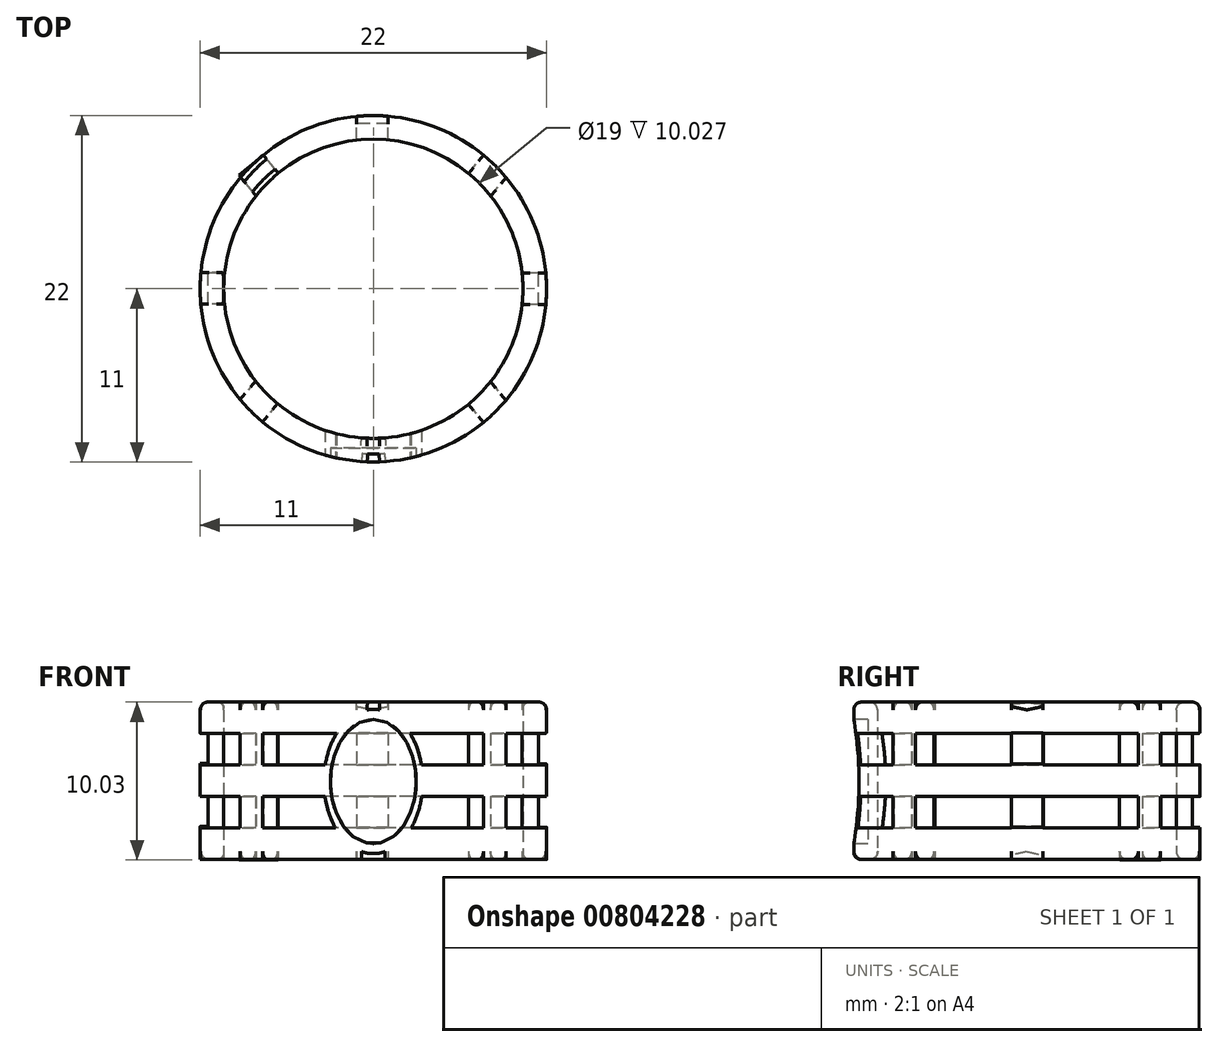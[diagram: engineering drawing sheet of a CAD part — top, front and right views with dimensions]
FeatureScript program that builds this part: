
annotation { "Feature Type Name" : "Feature", "Feature Type Description" : "" }
export const myFeature = defineFeature(function(context is Context, id is Id, definition is map)
    precondition{}
    {
        {
            var Q0;
            Q0=qCreatedBy(makeId("Top.planeOp"),FACE);
            var sketch = newSketch(context, id + "F0", { "sketchPlane" : qUnion([Q0])});
            skCircle(sketch, "E0", {"center": v(0, 0) * mm, "radius": 9.5 * mm});
            skCircle(sketch, "E1", {"center": v(0, 0) * mm, "radius": 11 * mm});
            skSolve(sketch);
        }
        {
            var Q0;
            Q0=makeQuery(id+"F0.imprint","IMPRINT",FACE,{"disambiguationData":[TD([[makeQuery(id+"F0.imprint","IMPRINT",EDGE,{"derivedFrom":sQuery(id+"F0.wireOp",EDGE,"E0")}),-1.0]])]});
            extrude(context, id + "F1", {"entities" : qUnion([Q0]), "depth" : 2 * mm, "offsetDistance" : 25.4 * mm});
        }
        {
            var Q0;
            Q0=qCreatedBy(makeId("Top.planeOp"),FACE);
            cPlane(context, id + "F2", {"entities" : qUnion([Q0]), "cplaneType" : CPlaneType.OFFSET, "offset" : 4 * mm, "width" : 152.4 * mm, "height" : 152.4 * mm});
        }
        {
            var Q0;
            Q0=qCreatedBy(id+"F2.planeOp",FACE);
            var sketch = newSketch(context, id + "F3", { "sketchPlane" : qUnion([Q0])});
            skCircle(sketch, "E2", {"center": v(0, 0) * mm, "radius": 9.5 * mm});
            skCircle(sketch, "E3", {"center": v(0, 0) * mm, "radius": 11 * mm});
            skSolve(sketch);
        }
        {
            var Q0;
            Q0=makeQuery(id+"F3.imprint","IMPRINT",FACE,{"disambiguationData":[TD([[makeQuery(id+"F3.imprint","IMPRINT",EDGE,{"derivedFrom":sQuery(id+"F3.wireOp",EDGE,"E2")}),-1.0]])]});
            extrude(context, id + "F4", {"entities" : qUnion([Q0]), "depth" : 2 * mm, "offsetDistance" : 25.4 * mm});
        }
        {
            var Q0;
            Q0=qCreatedBy(id+"F2.planeOp",FACE);
            cPlane(context, id + "F5", {"entities" : qUnion([Q0]), "cplaneType" : CPlaneType.OFFSET, "offset" : 4 * mm, "width" : 152.4 * mm, "height" : 152.4 * mm});
        }
        {
            var Q0;
            Q0=qCreatedBy(id+"F5.planeOp",FACE);
            var sketch = newSketch(context, id + "F6", { "sketchPlane" : qUnion([Q0])});
            skCircle(sketch, "E4", {"center": v(0, 0) * mm, "radius": 9.5 * mm});
            skCircle(sketch, "E5", {"center": v(0, 0) * mm, "radius": 11 * mm});
            skSolve(sketch);
        }
        {
            var Q0;
            Q0 = qSketchRegion(id + "F6", true);
            extrude(context, id + "F7", {"entities" : qUnion([Q0]), "depth" : 2 * mm, "offsetDistance" : 25.4 * mm});
        }
        {
            var Q0;
            Q0=qCreatedBy(makeId("Front.planeOp"),FACE);
            cPlane(context, id + "F8", {"entities" : qUnion([Q0]), "cplaneType" : CPlaneType.OFFSET, "offset" : 11 * mm, "width" : 152.4 * mm, "height" : 152.4 * mm});
        }
        {
            var Q0;
            Q0=qCreatedBy(id+"F8.planeOp",FACE);
            var sketch = newSketch(context, id + "F9", { "sketchPlane" : qUnion([Q0])});
            skEllipse(sketch, "E6", {"center": v(0, 4.95) * mm, "majorRadius": 4.58 * mm, "minorRadius": 3.14 * mm, "majorAxis": v(0, 1)});
            skEllipse(sketch, "E7", {"center": v(0, 4.95) * mm, "majorRadius": 4.36 * mm, "minorRadius": 2.48 * mm, "majorAxis": v(0, 1)});
            skSolve(sketch);
        }
        {
            var Q0;
            Q0=makeQuery(id+"F9.imprint","IMPRINT",FACE,{"disambiguationData":[TD([[makeQuery(id+"F9.imprint","IMPRINT",EDGE,{"derivedFrom":sQuery(id+"F9.wireOp",EDGE,"E7")}),1.0]])]});
            var Q1;
            Q1=makeQuery(id+"F9.imprint","IMPRINT",FACE,{"disambiguationData":[TD([[makeQuery(id+"F9.imprint","IMPRINT",EDGE,{"derivedFrom":sQuery(id+"F9.wireOp",EDGE,"E6")}),1.0]])]});
            extrude(context, id + "F10", {"entities" : qUnion([Q0, Q1]), "operationType" : NewBodyOperationType.ADD, "oppositeDirection" : true, "depth" : 2 * mm, "offsetDistance" : 25.4 * mm});
        }
        {
            var Q0;
            Q0=makeQuery(id+"F10.opExtrude","CAP_FACE",FACE,{"disambiguationData":[OSD([sQuery(id+"F9.wireOp",EDGE,"E6")])],"isStart":true});
            var sketch = newSketch(context, id + "F11", { "sketchPlane" : qUnion([Q0])});
            skEllipse(sketch, "E8", {"center": v(0, 4.95) * mm, "majorRadius": 3.96 * mm, "minorRadius": 2.72 * mm, "majorAxis": v(0, 1)});
            skSolve(sketch);
        }
        {
            var Q0;
            Q0=makeQuery(id+"F11.imprint","IMPRINT",FACE,{"disambiguationData":[TD([[makeQuery(id+"F11.imprint","IMPRINT",EDGE,{"derivedFrom":sQuery(id+"F11.wireOp",EDGE,"E8")}),1.0]])]});
            extrude(context, id + "F12", {"entities" : qUnion([Q0]), "operationType" : NewBodyOperationType.REMOVE, "oppositeDirection" : true, "depth" : .9 * mm, "offsetDistance" : 25.4 * mm});
        }
        {
            var Q0;
            Q0=qCreatedBy(makeId("Front.planeOp"),FACE);
            cPlane(context, id + "F13", {"entities" : qUnion([Q0]), "cplaneType" : CPlaneType.OFFSET, "offset" : 11 * mm, "oppositeDirection" : true, "width" : 152.4 * mm, "height" : 152.4 * mm});
        }
        {
            var Q0;
            Q0=qCreatedBy(id+"F13.planeOp",FACE);
            var sketch = newSketch(context, id + "F14", { "sketchPlane" : qUnion([Q0])});
            skLineSegment(sketch, "E9.bottom", {"start": v(0.94, 10) * mm, "end": v(-1.06, 10) * mm});
            skLineSegment(sketch, "E9.top", {"start": v(0.94, 0) * mm, "end": v(-1.06, 0) * mm});
            skLineSegment(sketch, "E9.left", {"start": v(0.94, 10) * mm, "end": v(0.94, 0) * mm});
            skLineSegment(sketch, "E9.right", {"start": v(-1.06, 10) * mm, "end": v(-1.06, 0) * mm});
            skSolve(sketch);
        }
        {
            var Q0;
            Q0=makeQuery(id+"F14.imprint","IMPRINT",FACE,{"disambiguationData":[TD([[makeQuery(id+"F14.imprint","IMPRINT",EDGE,{"derivedFrom":sQuery(id+"F14.wireOp",EDGE,"E9.bottom")}),1.0]])]});
            extrude(context, id + "F15", {"entities" : qUnion([Q0]), "operationType" : NewBodyOperationType.ADD, "depth" : 1.5 * mm, "offsetDistance" : 25.4 * mm});
        }
        {
            var Q0;
            Q0=makeQuery(id+"F7.opExtrude","CAP_EDGE",EDGE,{"disambiguationData":[OSD([sQuery(id+"F6.wireOp",EDGE,"E4")])],"isStart":false});
            var Q1;
            Q1=makeQuery(id+"F7.opExtrude","CAP_EDGE",EDGE,{"disambiguationData":[OSD([sQuery(id+"F6.wireOp",EDGE,"E5")])],"isStart":false});
            var Q2;
            Q2=makeQuery(id+"F1.opExtrude","CAP_EDGE",EDGE,{"disambiguationData":[OSD([sQuery(id+"F0.wireOp",EDGE,"E1")])],"isStart":true});
            var Q3;
            Q3=makeQuery(id+"F1.opExtrude","CAP_EDGE",EDGE,{"disambiguationData":[OSD([sQuery(id+"F0.wireOp",EDGE,"E0")])],"isStart":true});
            fillet(context, id + "F16", {"entities" : qUnion([Q0, Q1, Q2, Q3]), "radius" : .5 * mm, "tangentPropagation" : true, "allowEdgeOverflow" : false});
        }
        {
            var Q0;
            Q0=makeQuery(id+"F15.opExtrude","CAP_EDGE",EDGE,{"disambiguationData":[OSD([sQuery(id+"F14.wireOp",EDGE,"E9.bottom")])],"isStart":true});
            fillet(context, id + "F17", {"entities" : qUnion([Q0]), "radius" : .5 * mm, "tangentPropagation" : true, "allowEdgeOverflow" : false});
        }
        {
            var Q0;
            Q0=qCreatedBy(makeId("Right.planeOp"),FACE);
            cPlane(context, id + "F18", {"entities" : qUnion([Q0]), "cplaneType" : CPlaneType.OFFSET, "offset" : 11 * mm, "width" : 152.4 * mm, "height" : 152.4 * mm});
        }
        {
            var Q0;
            Q0=qCreatedBy(id+"F18.planeOp",FACE);
            var sketch = newSketch(context, id + "F19", { "sketchPlane" : qUnion([Q0])});
            skLineSegment(sketch, "E10.bottom", {"start": v(-1, 0) * mm, "end": v(1, 0) * mm});
            skLineSegment(sketch, "E10.top", {"start": v(-1, 10) * mm, "end": v(1, 10) * mm});
            skLineSegment(sketch, "E10.left", {"start": v(-1, 0) * mm, "end": v(-1, 10) * mm});
            skLineSegment(sketch, "E10.right", {"start": v(1, 0) * mm, "end": v(1, 10) * mm});
            skSolve(sketch);
        }
        {
            var Q0;
            Q0=makeQuery(id+"F19.imprint","IMPRINT",FACE,{"disambiguationData":[TD([[makeQuery(id+"F19.imprint","IMPRINT",EDGE,{"derivedFrom":sQuery(id+"F19.wireOp",EDGE,"E10.bottom")}),1.0]])]});
            extrude(context, id + "F20", {"entities" : qUnion([Q0]), "operationType" : NewBodyOperationType.ADD, "oppositeDirection" : true, "depth" : 1.7 * mm, "offsetDistance" : 25.4 * mm});
        }
        {
            var Q0;
            Q0=qCreatedBy(makeId("Right.planeOp"),FACE);
            cPlane(context, id + "F21", {"entities" : qUnion([Q0]), "cplaneType" : CPlaneType.OFFSET, "offset" : 11 * mm, "oppositeDirection" : true, "width" : 152.4 * mm, "height" : 152.4 * mm});
        }
        {
            var Q0;
            Q0=qCreatedBy(id+"F21.planeOp",FACE);
            var sketch = newSketch(context, id + "F22", { "sketchPlane" : qUnion([Q0])});
            skLineSegment(sketch, "E11.bottom", {"start": v(1.04, 10) * mm, "end": v(-0.96, 10) * mm});
            skLineSegment(sketch, "E11.top", {"start": v(1.04, 0) * mm, "end": v(-0.96, 0) * mm});
            skLineSegment(sketch, "E11.left", {"start": v(1.04, 10) * mm, "end": v(1.04, 0) * mm});
            skLineSegment(sketch, "E11.right", {"start": v(-0.96, 10) * mm, "end": v(-0.96, 0) * mm});
            skSolve(sketch);
        }
        {
            var Q0;
            Q0=makeQuery(id+"F22.imprint","IMPRINT",FACE,{"disambiguationData":[TD([[makeQuery(id+"F22.imprint","IMPRINT",EDGE,{"derivedFrom":sQuery(id+"F22.wireOp",EDGE,"E11.bottom")}),1.0]])]});
            extrude(context, id + "F23", {"entities" : qUnion([Q0]), "operationType" : NewBodyOperationType.ADD, "depth" : 1.5 * mm, "offsetDistance" : 25.4 * mm});
        }
        {
            var Q0;
            Q0=makeQuery(id+"F20.opExtrude","CAP_EDGE",EDGE,{"disambiguationData":[OSD([sQuery(id+"F19.wireOp",EDGE,"E10.top")])],"isStart":false});
            var Q1;
            Q1=makeQuery(id+"F20.opExtrude","CAP_EDGE",EDGE,{"disambiguationData":[OSD([sQuery(id+"F19.wireOp",EDGE,"E10.top")])],"isStart":true});
            var Q2;
            Q2=makeQuery(id+"F23.opExtrude","CAP_EDGE",EDGE,{"disambiguationData":[OSD([sQuery(id+"F22.wireOp",EDGE,"E11.bottom")])],"isStart":true});
            fillet(context, id + "F24", {"entities" : qUnion([Q0, Q1, Q2]), "radius" : .5 * mm, "tangentPropagation" : true, "allowEdgeOverflow" : false});
        }
        {
            var Q0;
            Q0=makeQuery(id+"F23.opExtrude","CAP_EDGE",EDGE,{"disambiguationData":[OSD([sQuery(id+"F22.wireOp",EDGE,"E11.bottom")])],"isStart":false});
            fillet(context, id + "F25", {"entities" : qUnion([Q0]), "radius" : .4 * mm, "tangentPropagation" : true, "allowEdgeOverflow" : false});
        }
        {
            var Q0;
            Q0=makeQuery(id+"F20.opExtrude","CAP_FACE",FACE,{"disambiguationData":[OSD([sQuery(id+"F19.wireOp",EDGE,"E10.bottom"),sQuery(id+"F19.wireOp",EDGE,"E10.top"),sQuery(id+"F19.wireOp",EDGE,"E10.left"),sQuery(id+"F19.wireOp",EDGE,"E10.right")])],"isStart":true});
            var sketch = newSketch(context, id + "F26", { "sketchPlane" : qUnion([Q0])});
            skLineSegment(sketch, "E12.bottom", {"start": v(-1, 8.03) * mm, "end": v(1, 8.03) * mm});
            skLineSegment(sketch, "E12.top", {"start": v(-1, 6.06) * mm, "end": v(1, 6.06) * mm});
            skLineSegment(sketch, "E12.left", {"start": v(-1, 8.03) * mm, "end": v(-1, 6.06) * mm});
            skLineSegment(sketch, "E12.right", {"start": v(1, 8.03) * mm, "end": v(1, 6.06) * mm});
            skLineSegment(sketch, "E13.bottom", {"start": v(-1, 4.02) * mm, "end": v(1, 4.02) * mm});
            skLineSegment(sketch, "E13.top", {"start": v(-1, 2.05) * mm, "end": v(1, 2.05) * mm});
            skLineSegment(sketch, "E13.left", {"start": v(-1, 4.02) * mm, "end": v(-1, 2.05) * mm});
            skLineSegment(sketch, "E13.right", {"start": v(1, 4.02) * mm, "end": v(1, 2.05) * mm});
            skSolve(sketch);
        }
        {
            var Q0;
            Q0=makeQuery(id+"F26.imprint","IMPRINT",FACE,{"disambiguationData":[TD([[makeQuery(id+"F26.imprint","IMPRINT",EDGE,{"derivedFrom":sQuery(id+"F26.wireOp",EDGE,"E12.bottom")}),-1.0]])]});
            var Q1;
            Q1=makeQuery(id+"F26.imprint","IMPRINT",FACE,{"disambiguationData":[TD([[makeQuery(id+"F26.imprint","IMPRINT",EDGE,{"derivedFrom":sQuery(id+"F26.wireOp",EDGE,"E13.bottom")}),-1.0]])]});
            extrude(context, id + "F27", {"entities" : qUnion([Q0, Q1]), "operationType" : NewBodyOperationType.REMOVE, "oppositeDirection" : true, "depth" : .5 * mm, "offsetDistance" : 25.4 * mm});
        }
        {
            var Q0;
            Q0=makeQuery(id+"F15.opExtrude","CAP_FACE",FACE,{"disambiguationData":[OSD([sQuery(id+"F14.wireOp",EDGE,"E9.bottom"),sQuery(id+"F14.wireOp",EDGE,"E9.top"),sQuery(id+"F14.wireOp",EDGE,"E9.left"),sQuery(id+"F14.wireOp",EDGE,"E9.right")])],"isStart":true});
            var sketch = newSketch(context, id + "F28", { "sketchPlane" : qUnion([Q0])});
            skLineSegment(sketch, "E14.bottom", {"start": v(-0.94, 8.03) * mm, "end": v(1.06, 8.03) * mm});
            skLineSegment(sketch, "E14.top", {"start": v(-0.94, 6.01) * mm, "end": v(1.06, 6.01) * mm});
            skLineSegment(sketch, "E14.left", {"start": v(-0.94, 8.03) * mm, "end": v(-0.94, 6.01) * mm});
            skLineSegment(sketch, "E14.right", {"start": v(1.06, 8.03) * mm, "end": v(1.06, 6.01) * mm});
            skLineSegment(sketch, "E15.bottom", {"start": v(1.06, 4) * mm, "end": v(-0.94, 4) * mm});
            skLineSegment(sketch, "E15.top", {"start": v(1.06, 2.05) * mm, "end": v(-0.94, 2.05) * mm});
            skLineSegment(sketch, "E15.left", {"start": v(1.06, 4) * mm, "end": v(1.06, 2.05) * mm});
            skLineSegment(sketch, "E15.right", {"start": v(-0.94, 4) * mm, "end": v(-0.94, 2.05) * mm});
            skSolve(sketch);
        }
        {
            var Q0;
            Q0=makeQuery(id+"F28.imprint","IMPRINT",FACE,{"disambiguationData":[TD([[makeQuery(id+"F28.imprint","IMPRINT",EDGE,{"derivedFrom":sQuery(id+"F28.wireOp",EDGE,"E14.bottom")}),-1.0]])]});
            var Q1;
            Q1=makeQuery(id+"F28.imprint","IMPRINT",FACE,{"disambiguationData":[TD([[makeQuery(id+"F28.imprint","IMPRINT",EDGE,{"derivedFrom":sQuery(id+"F28.wireOp",EDGE,"E15.bottom")}),1.0]])]});
            extrude(context, id + "F29", {"entities" : qUnion([Q0, Q1]), "operationType" : NewBodyOperationType.REMOVE, "oppositeDirection" : true, "depth" : .5 * mm, "offsetDistance" : 25.4 * mm});
        }
        {
            var Q0;
            Q0=makeQuery(id+"F23.opExtrude","CAP_FACE",FACE,{"disambiguationData":[OSD([sQuery(id+"F22.wireOp",EDGE,"E11.bottom"),sQuery(id+"F22.wireOp",EDGE,"E11.top"),sQuery(id+"F22.wireOp",EDGE,"E11.left"),sQuery(id+"F22.wireOp",EDGE,"E11.right")])],"isStart":true});
            var sketch = newSketch(context, id + "F30", { "sketchPlane" : qUnion([Q0])});
            skLineSegment(sketch, "E16.bottom", {"start": v(-1.04, 8) * mm, "end": v(0.96, 8) * mm});
            skLineSegment(sketch, "E16.top", {"start": v(-1.04, 6.1) * mm, "end": v(0.96, 6.1) * mm});
            skLineSegment(sketch, "E16.left", {"start": v(-1.04, 8) * mm, "end": v(-1.04, 6.1) * mm});
            skLineSegment(sketch, "E16.right", {"start": v(0.96, 8) * mm, "end": v(0.96, 6.1) * mm});
            skLineSegment(sketch, "E17.bottom", {"start": v(0.96, 2.1) * mm, "end": v(-1.04, 2.1) * mm});
            skLineSegment(sketch, "E17.top", {"start": v(0.96, 4) * mm, "end": v(-1.04, 4) * mm});
            skLineSegment(sketch, "E17.left", {"start": v(0.96, 2.1) * mm, "end": v(0.96, 4) * mm});
            skLineSegment(sketch, "E17.right", {"start": v(-1.04, 2.1) * mm, "end": v(-1.04, 4) * mm});
            skSolve(sketch);
        }
        {
            var Q0;
            Q0=makeQuery(id+"F30.imprint","IMPRINT",FACE,{"disambiguationData":[TD([[makeQuery(id+"F30.imprint","IMPRINT",EDGE,{"derivedFrom":sQuery(id+"F30.wireOp",EDGE,"E16.bottom")}),-1.0]])]});
            var Q1;
            Q1=makeQuery(id+"F30.imprint","IMPRINT",FACE,{"disambiguationData":[TD([[makeQuery(id+"F30.imprint","IMPRINT",EDGE,{"derivedFrom":sQuery(id+"F30.wireOp",EDGE,"E17.bottom")}),-1.0]])]});
            extrude(context, id + "F31", {"entities" : qUnion([Q0, Q1]), "operationType" : NewBodyOperationType.REMOVE, "oppositeDirection" : true, "depth" : .5 * mm, "offsetDistance" : 25.4 * mm});
        }
        {
            var Q0;
            Q0=qCreatedBy(makeId("Top.planeOp"),FACE);
            var sketch = newSketch(context, id + "F32", { "sketchPlane" : qUnion([Q0])});
            skCircle(sketch, "E18", {"center": v(0, 0) * mm, "radius": 9.5 * mm});
            skSolve(sketch);
        }
        {
            var Q0;
            Q0=qCreatedBy(makeId("Top.planeOp"),FACE);
            var sketch = newSketch(context, id + "F33", { "sketchPlane" : qUnion([Q0])});
            skCircle(sketch, "E19", {"center": v(0, 0) * mm, "radius": 11 * mm});
            skCircle(sketch, "E20", {"center": v(0, 0) * mm, "radius": 11.5 * mm});
            skSolve(sketch);
        }
        {
            var Q0;
            Q0=makeQuery(id+"F33.imprint","IMPRINT",FACE,{"disambiguationData":[TD([[makeQuery(id+"F33.imprint","IMPRINT",EDGE,{"derivedFrom":sQuery(id+"F33.wireOp",EDGE,"E19")}),-1.0]])]});
            extrude(context, id + "F34", {"entities" : qUnion([Q0]), "operationType" : NewBodyOperationType.REMOVE, "depth" : 25.4 * mm, "offsetDistance" : 25.4 * mm});
        }
        {
            var Q0;
            {var subQ0=sQuery(id+"F3.wireOp",EDGE,"E3");var subQ3=makeQuery(id+"F10.opExtrude","SWEPT_FACE",FACE,{"disambiguationData":[OSD([sQuery(id+"F9.wireOp",EDGE,"E6")])]});Q0=makeQuery(id+"F23.boolean.opBoolean","SPLIT",EDGE,{"disambiguationData":[TD([subQ3])],"derivedFrom":makeQuery(id+"F15.boolean.opBoolean","SPLIT",EDGE,{"disambiguationData":[TD([makeQuery(id+"F15.opExtrude","SWEPT_FACE",FACE,{"disambiguationData":[OSD([sQuery(id+"F14.wireOp",EDGE,"E9.right")])]})])],"derivedFrom":makeQuery(id+"F4.opExtrude","CAP_EDGE",EDGE,{"disambiguationData":[OSD([subQ0])],"isStart":false})})});}
            cPoint(context, id + "F35", {"entities" : qUnion([Q0]), "parameter" : 0.5});
        }
        {
            var Q0;
            {var subQ0=sQuery(id+"F3.wireOp",EDGE,"E3");var subQ3=makeQuery(id+"F10.opExtrude","SWEPT_FACE",FACE,{"disambiguationData":[OSD([sQuery(id+"F9.wireOp",EDGE,"E6")])]});Q0=makeQuery(id+"F23.boolean.opBoolean","SPLIT",EDGE,{"disambiguationData":[TD([subQ3])],"derivedFrom":makeQuery(id+"F15.boolean.opBoolean","SPLIT",EDGE,{"disambiguationData":[TD([makeQuery(id+"F15.opExtrude","SWEPT_FACE",FACE,{"disambiguationData":[OSD([sQuery(id+"F14.wireOp",EDGE,"E9.right")])]})])],"derivedFrom":makeQuery(id+"F4.opExtrude","CAP_EDGE",EDGE,{"disambiguationData":[OSD([subQ0])],"isStart":false})})});}
            var Q1;
            Q1 = qCreatedBy(id + "F35" ,VERTEX);
            cPlane(context, id + "F36", {"entities" : qUnion([Q0, Q1]), "cplaneType" : CPlaneType.CURVE_POINT, "offset" : 25.4 * mm, "width" : 152.4 * mm, "height" : 152.4 * mm});
        }
        {
            var Q0;
            Q0=qCreatedBy(id+"F36.planeOp",FACE);
            cPlane(context, id + "F37", {"entities" : qUnion([Q0]), "cplaneType" : CPlaneType.OFFSET, "offset" : 11 * mm, "oppositeDirection" : true, "width" : 152.4 * mm, "height" : 152.4 * mm});
        }
        {
            var Q0;
            Q0=qCreatedBy(id+"F37.planeOp",FACE);
            var sketch = newSketch(context, id + "F38", { "sketchPlane" : qUnion([Q0])});
            skLineSegment(sketch, "E21.bottom", {"start": v(0, 9.97) * mm, "end": v(-2, 9.97) * mm});
            skLineSegment(sketch, "E21.top", {"start": v(0, -0.03) * mm, "end": v(-2, -0.03) * mm});
            skLineSegment(sketch, "E21.left", {"start": v(0, 9.97) * mm, "end": v(0, -0.03) * mm});
            skLineSegment(sketch, "E21.right", {"start": v(-2, 9.97) * mm, "end": v(-2, -0.03) * mm});
            skSolve(sketch);
        }
        {
            var Q0;
            Q0=makeQuery(id+"F38.imprint","IMPRINT",FACE,{"disambiguationData":[TD([[makeQuery(id+"F38.imprint","IMPRINT",EDGE,{"derivedFrom":sQuery(id+"F38.wireOp",EDGE,"E21.bottom")}),1.0]])]});
            extrude(context, id + "F39", {"entities" : qUnion([Q0]), "operationType" : NewBodyOperationType.ADD, "depth" : 3 * mm, "offsetDistance" : 25.4 * mm});
        }
        {
            var Q0;
            Q0=qCreatedBy(id+"F36.planeOp",FACE);
            cPlane(context, id + "F40", {"entities" : qUnion([Q0]), "cplaneType" : CPlaneType.OFFSET, "offset" : 11 * mm, "width" : 152.4 * mm, "height" : 152.4 * mm});
        }
        {
            var Q0;
            Q0=qCreatedBy(id+"F40.planeOp",FACE);
            var sketch = newSketch(context, id + "F41", { "sketchPlane" : qUnion([Q0])});
            skLineSegment(sketch, "E22.bottom", {"start": v(0, 10) * mm, "end": v(2, 10) * mm});
            skLineSegment(sketch, "E22.top", {"start": v(0, 0) * mm, "end": v(2, 0) * mm});
            skLineSegment(sketch, "E22.left", {"start": v(0, 10) * mm, "end": v(0, 0) * mm});
            skLineSegment(sketch, "E22.right", {"start": v(2, 10) * mm, "end": v(2, 0) * mm});
            skSolve(sketch);
        }
        {
            var Q0;
            {var subQ0=sQuery(id+"F3.wireOp",EDGE,"E3");var subQ3=makeQuery(id+"F10.opExtrude","SWEPT_FACE",FACE,{"disambiguationData":[OSD([sQuery(id+"F9.wireOp",EDGE,"E6")])]});Q0=makeQuery(id+"F20.boolean.opBoolean","SPLIT",EDGE,{"disambiguationData":[TD([subQ3])],"derivedFrom":makeQuery(id+"F15.boolean.opBoolean","SPLIT",EDGE,{"disambiguationData":[TD([makeQuery(id+"F15.opExtrude","SWEPT_FACE",FACE,{"disambiguationData":[OSD([sQuery(id+"F14.wireOp",EDGE,"E9.left")])]})])],"derivedFrom":makeQuery(id+"F4.opExtrude","CAP_EDGE",EDGE,{"disambiguationData":[OSD([subQ0])],"isStart":false})})});}
            cPoint(context, id + "F42", {"entities" : qUnion([Q0]), "parameter" : 0.5});
        }
        {
            var Q0;
            Q0 = qCreatedBy(id + "F42" ,VERTEX);
            var Q1;
            {var subQ0=sQuery(id+"F3.wireOp",EDGE,"E3");var subQ3=makeQuery(id+"F10.opExtrude","SWEPT_FACE",FACE,{"disambiguationData":[OSD([sQuery(id+"F9.wireOp",EDGE,"E6")])]});Q1=makeQuery(id+"F20.boolean.opBoolean","SPLIT",EDGE,{"disambiguationData":[TD([subQ3])],"derivedFrom":makeQuery(id+"F15.boolean.opBoolean","SPLIT",EDGE,{"disambiguationData":[TD([makeQuery(id+"F15.opExtrude","SWEPT_FACE",FACE,{"disambiguationData":[OSD([sQuery(id+"F14.wireOp",EDGE,"E9.left")])]})])],"derivedFrom":makeQuery(id+"F4.opExtrude","CAP_EDGE",EDGE,{"disambiguationData":[OSD([subQ0])],"isStart":false})})});}
            cPlane(context, id + "F43", {"entities" : qUnion([Q0, Q1]), "cplaneType" : CPlaneType.CURVE_POINT, "offset" : 25.4 * mm, "width" : 152.4 * mm, "height" : 152.4 * mm});
        }
        {
            var Q0;
            Q0 = qSketchRegion(id + "F41", true);
            extrude(context, id + "F44", {"entities" : qUnion([Q0]), "operationType" : NewBodyOperationType.ADD, "oppositeDirection" : true, "depth" : 3 * mm, "offsetDistance" : 25.4 * mm});
        }
        {
            var Q0;
            Q0=qCreatedBy(id+"F43.planeOp",FACE);
            cPlane(context, id + "F45", {"entities" : qUnion([Q0]), "cplaneType" : CPlaneType.OFFSET, "offset" : 11 * mm, "oppositeDirection" : true, "width" : 152.4 * mm, "height" : 152.4 * mm});
        }
        {
            var Q0;
            Q0=qCreatedBy(id+"F45.planeOp",FACE);
            var sketch = newSketch(context, id + "F46", { "sketchPlane" : qUnion([Q0])});
            skLineSegment(sketch, "E23.bottom", {"start": v(2.04, 10) * mm, "end": v(0.04, 10) * mm});
            skLineSegment(sketch, "E23.top", {"start": v(2.04, 0) * mm, "end": v(0.04, 0) * mm});
            skLineSegment(sketch, "E23.left", {"start": v(2.04, 10) * mm, "end": v(2.04, 0) * mm});
            skLineSegment(sketch, "E23.right", {"start": v(0.04, 10) * mm, "end": v(0.04, 0) * mm});
            skSolve(sketch);
        }
        {
            var Q0;
            Q0=qCreatedBy(id+"F43.planeOp",FACE);
            cPlane(context, id + "F47", {"entities" : qUnion([Q0]), "cplaneType" : CPlaneType.OFFSET, "offset" : 11 * mm, "width" : 152.4 * mm, "height" : 152.4 * mm});
        }
        {
            var Q0;
            Q0=qCreatedBy(id+"F47.planeOp",FACE);
            var sketch = newSketch(context, id + "F48", { "sketchPlane" : qUnion([Q0])});
            skLineSegment(sketch, "E24.bottom", {"start": v(-2, 10) * mm, "end": v(0, 10) * mm});
            skLineSegment(sketch, "E24.top", {"start": v(-2, 0) * mm, "end": v(0, 0) * mm});
            skLineSegment(sketch, "E24.left", {"start": v(-2, 10) * mm, "end": v(-2, 0) * mm});
            skLineSegment(sketch, "E24.right", {"start": v(0, 10) * mm, "end": v(0, 0) * mm});
            skSolve(sketch);
        }
        {
            var Q0;
            Q0=makeQuery(id+"F48.imprint","IMPRINT",FACE,{"disambiguationData":[TD([[makeQuery(id+"F48.imprint","IMPRINT",EDGE,{"derivedFrom":sQuery(id+"F48.wireOp",EDGE,"E24.bottom")}),-1.0]])]});
            extrude(context, id + "F49", {"entities" : qUnion([Q0]), "operationType" : NewBodyOperationType.ADD, "oppositeDirection" : true, "depth" : 3 * mm, "offsetDistance" : 25.4 * mm});
        }
        {
            var Q0;
            Q0=makeQuery(id+"F46.imprint","IMPRINT",FACE,{"disambiguationData":[TD([[makeQuery(id+"F46.imprint","IMPRINT",EDGE,{"derivedFrom":sQuery(id+"F46.wireOp",EDGE,"E23.bottom")}),1.0]])]});
            extrude(context, id + "F50", {"entities" : qUnion([Q0]), "operationType" : NewBodyOperationType.ADD, "depth" : 3 * mm, "offsetDistance" : 25.4 * mm});
        }
        {
            var Q0;
            Q0=qCreatedBy(makeId("Top.planeOp"),FACE);
            var sketch = newSketch(context, id + "F51", { "sketchPlane" : qUnion([Q0])});
            skCircle(sketch, "E25", {"center": v(0, 0) * mm, "radius": 11.5 * mm});
            skCircle(sketch, "E26", {"center": v(0, 0) * mm, "radius": 11 * mm});
            skSolve(sketch);
        }
        {
            var Q0;
            Q0=makeQuery(id+"F51.imprint","IMPRINT",FACE,{"disambiguationData":[TD([[makeQuery(id+"F51.imprint","IMPRINT",EDGE,{"derivedFrom":sQuery(id+"F51.wireOp",EDGE,"E25")}),1.0]])]});
            extrude(context, id + "F52", {"entities" : qUnion([Q0]), "operationType" : NewBodyOperationType.REMOVE, "depth" : 25.4 * mm, "offsetDistance" : 25.4 * mm});
        }
        {
            var Q0;
            Q0=makeQuery(id+"F32.imprint","IMPRINT",FACE,{"disambiguationData":[TD([[makeQuery(id+"F32.imprint","IMPRINT",EDGE,{"derivedFrom":sQuery(id+"F32.wireOp",EDGE,"E18")}),1.0]])]});
            extrude(context, id + "F53", {"entities" : qUnion([Q0]), "operationType" : NewBodyOperationType.REMOVE, "depth" : 10 * mm, "offsetDistance" : 25.4 * mm});
        }
        {
            var Q0;
            Q0=qCreatedBy(makeId("Top.planeOp"),FACE);
            var sketch = newSketch(context, id + "F54", { "sketchPlane" : qUnion([Q0])});
            skCircle(sketch, "E27", {"center": v(0, 0) * mm, "radius": 9.5 * mm});
            skSolve(sketch);
        }
        {
            var Q0;
            Q0=makeQuery(id+"F54.imprint","IMPRINT",FACE,{"disambiguationData":[TD([[makeQuery(id+"F54.imprint","IMPRINT",EDGE,{"derivedFrom":sQuery(id+"F54.wireOp",EDGE,"E27")}),1.0]])]});
            extrude(context, id + "F55", {"entities" : qUnion([Q0]), "operationType" : NewBodyOperationType.REMOVE, "oppositeDirection" : true, "depth" : 25.4 * mm, "offsetDistance" : 25.4 * mm});
        }
    });
